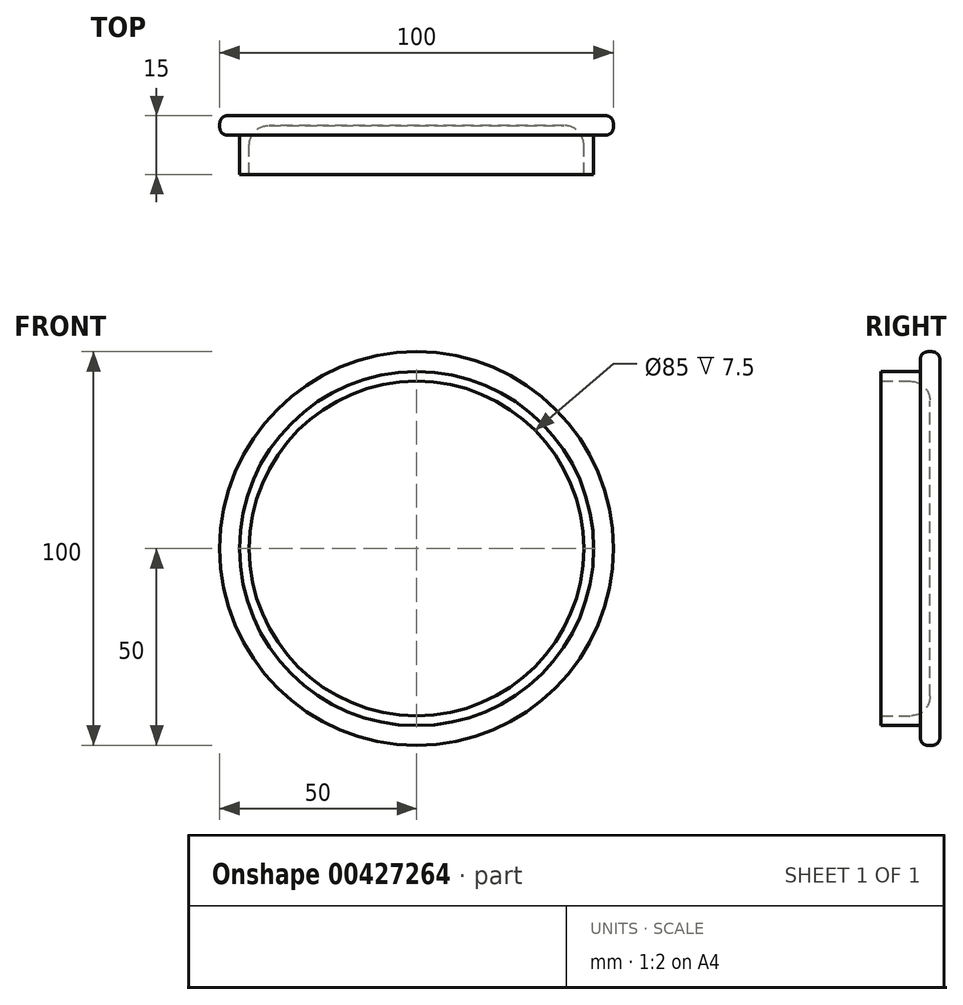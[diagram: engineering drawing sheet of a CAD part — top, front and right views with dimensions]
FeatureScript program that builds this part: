
annotation { "Feature Type Name" : "Feature", "Feature Type Description" : "" }
export const myFeature = defineFeature(function(context is Context, id is Id, definition is map)
    precondition{}
    {
        {
            var Q0;
            Q0=qCreatedBy(makeId("Front.planeOp"),FACE);
            var sketch = newSketch(context, id + "F0", { "sketchPlane" : qUnion([Q0])});
            skCircle(sketch, "E0", {"center": v(0, 0) * mm, "radius": 50 * mm});
            skSolve(sketch);
        }
        {
            var Q0;
            Q0 = qSketchRegion(id + "F0", true);
            extrude(context, id + "F1", {"entities" : qUnion([Q0]), "depth" : 5 * mm});
        }
        {
            var Q0;
            Q0=qCreatedBy(makeId("Front.planeOp"),FACE);
            var sketch = newSketch(context, id + "F2", { "sketchPlane" : qUnion([Q0])});
            skCircle(sketch, "E1", {"center": v(0, 0) * mm, "radius": 45 * mm});
            skSolve(sketch);
        }
        {
            var Q0;
            Q0=makeQuery(id+"F1.opExtrude","CAP_EDGE",EDGE,{"disambiguationData":[OSD([sQuery(id+"F0.wireOp",EDGE,"E0")])],"isStart":false});
            var Q1;
            Q1=makeQuery(id+"F1.opExtrude","CAP_EDGE",EDGE,{"disambiguationData":[OSD([sQuery(id+"F0.wireOp",EDGE,"E0")])],"isStart":true});
            fillet(context, id + "F3", {"entities" : qUnion([Q0, Q1]), "radius" : 2 * mm, "tangentPropagation" : true, "allowEdgeOverflow" : false});
        }
        {
            var Q0;
            Q0 = qSketchRegion(id + "F2", true);
            extrude(context, id + "F4", {"entities" : qUnion([Q0]), "operationType" : NewBodyOperationType.ADD, "depth" : 15 * mm});
        }
        {
            var Q0;
            Q0=makeQuery(id+"F4.opExtrude","CAP_FACE",FACE,{"disambiguationData":[OSD([sQuery(id+"F2.wireOp",EDGE,"E1")])],"isStart":false});
            shell(context, id + "F5", {"entities" : qUnion([Q0]), "thickness" : 2.5 * mm});
        }
        {
            var Q0;
            Q0=makeQuery(id+"F5.opShell","OFFSET_EDGE",EDGE,{"disambiguationData":[OSD([sQuery(id+"F0.wireOp",EDGE,"E0"),sQuery(id+"F2.wireOp",EDGE,"E1")])]});
            fillet(context, id + "F6", {"entities" : qUnion([Q0]), "radius" : 5 * mm, "tangentPropagation" : true, "allowEdgeOverflow" : false});
        }
    });
